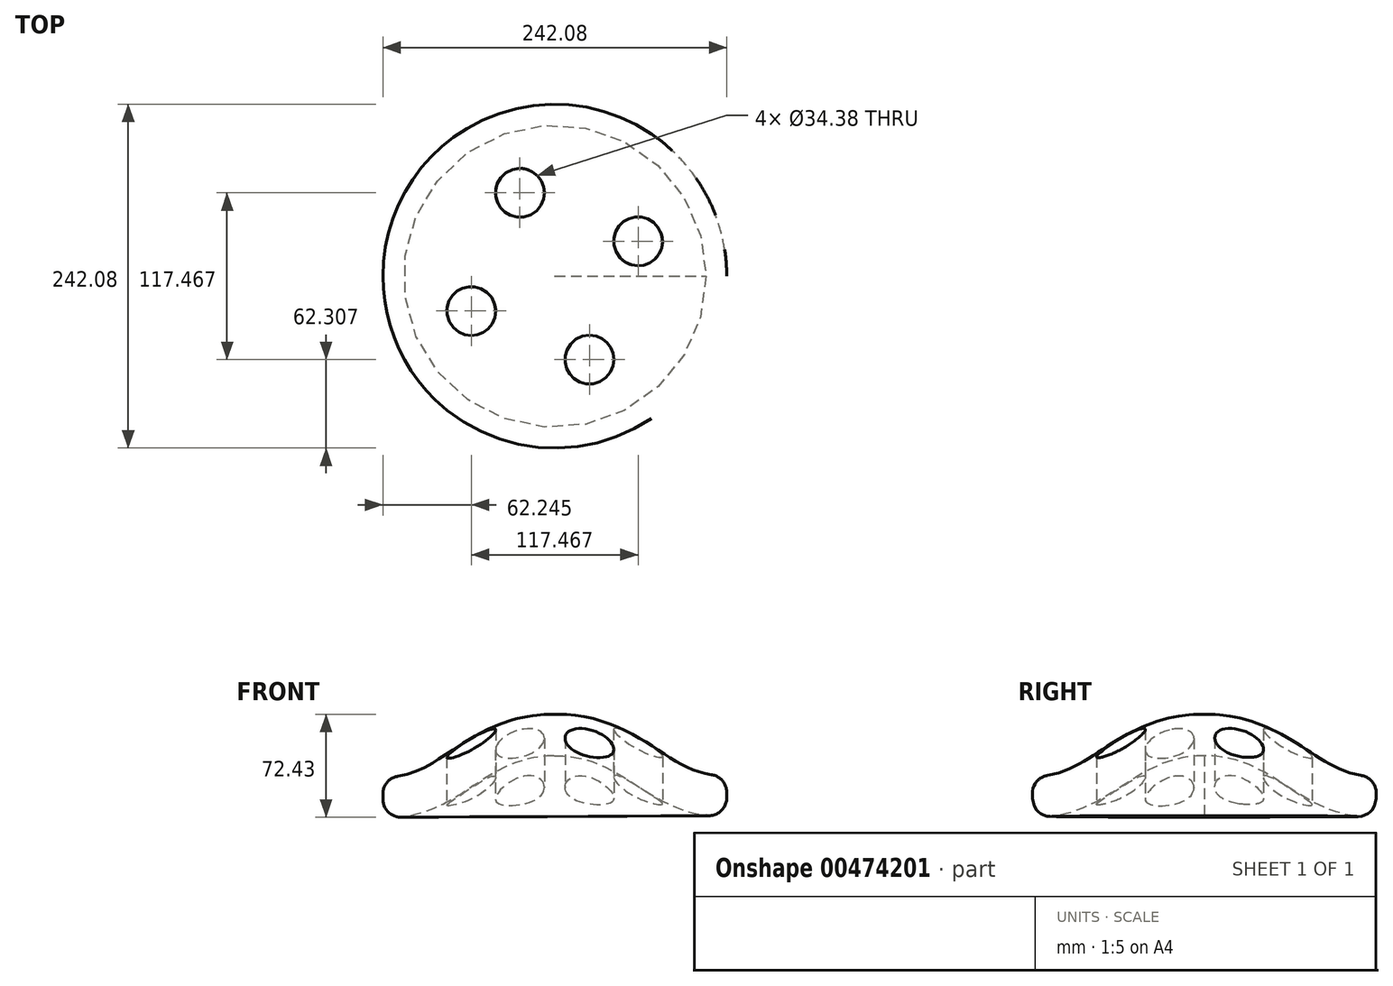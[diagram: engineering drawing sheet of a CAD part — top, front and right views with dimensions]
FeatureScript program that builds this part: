
annotation { "Feature Type Name" : "Feature", "Feature Type Description" : "" }
export const myFeature = defineFeature(function(context is Context, id is Id, definition is map)
    precondition{}
    {
        {
            var Q0;
            Q0=qCreatedBy(makeId("Front.planeOp"),FACE);
            var sketch = newSketch(context, id + "F0", { "sketchPlane" : qUnion([Q0])});
            skFitSpline(sketch, "E0", {"points": [v(-152.81, 0) * mm, v(-31.61, 43.06) * mm], "startDerivative": vector(155.87, -0.76) * mm, "endDerivative": vector(171.09, -0.36) * mm});
            skFitSpline(sketch, "E1.0", {"points": [v(-152.95, -29.15) * mm, v(-148.69, -29.17) * mm, v(-140.4, -28.76) * mm, v(-128.76, -26.9) * mm, v(-118.01, -23.95) * mm, v(-108.25, -20.2) * mm, v(-99.49, -15.95) * mm, v(-91.64, -11.5) * mm, v(-84.58, -7.09) * mm, v(-78.17, -2.92) * mm, v(-72.28, 0.89) * mm, v(-66.76, 4.23) * mm, v(-61.5, 7.07) * mm, v(-56.35, 9.42) * mm, v(-51.1, 11.3) * mm, v(-45.47, 12.73) * mm, v(-39.17, 13.68) * mm, v(-34.31, 13.92) * mm, v(-31.67, 13.91) * mm]});
            skLineSegment(sketch, "E2", {"start": v(-31.61, 43.06) * mm, "end": v(-31.67, 13.91) * mm});
            skLineSegment(sketch, "E3", {"start": v(-152.81, 0) * mm, "end": v(-152.95, -29.15) * mm});
            skSolve(sketch);
        }
        {
            var Q0;
            Q0=makeQuery(id+"F0.imprint","IMPRINT",FACE,{"disambiguationData":[TD([[makeQuery(id+"F0.imprint","IMPRINT",EDGE,{"derivedFrom":sQuery(id+"F0.wireOp",EDGE,"E0")}),-1.0]])]});
            var Q1;
            Q1=sQuery(id+"F0.wireOp",EDGE,"E3");
            revolve(context, id + "F1", {"entities" : qUnion([Q0]), "axis" : qUnion([Q1]), "revolveType" : RevolveType.FULL});
        }
        {
            var Q0;
            Q0=qCreatedBy(makeId("Top.planeOp"),FACE);
            var sketch = newSketch(context, id + "F2", { "sketchPlane" : qUnion([Q0])});
            skEllipse(sketch, "E4.0", {"center": v(-152.74, 0) * mm, "majorRadius": 121.07 * mm, "minorRadius": 121.07 * mm, "majorAxis": v(0, -1)});
            skCircle(sketch, "E5", {"center": v(-177.24, -58.73) * mm, "radius": 17.2 * mm});
            skCircle(sketch, "E6.1.0", {"center": v(-94, -24.5) * mm, "radius": 17.2 * mm});
            skCircle(sketch, "E6.2.0", {"center": v(-128.24, 58.73) * mm, "radius": 17.2 * mm});
            skCircle(sketch, "E7.1.3.0", {"center": v(-211.48, 24.5) * mm, "radius": 17.2 * mm});
            skSolve(sketch);
        }
        {
            var Q0;
            Q0=makeQuery(id+"F2.imprint","IMPRINT",FACE,{"disambiguationData":[TD([[makeQuery(id+"F2.imprint","IMPRINT",EDGE,{"derivedFrom":sQuery(id+"F2.wireOp",EDGE,"E6.2.0")}),1.0]])]});
            var Q1;
            Q1=makeQuery(id+"F2.imprint","IMPRINT",FACE,{"disambiguationData":[TD([[makeQuery(id+"F2.imprint","IMPRINT",EDGE,{"derivedFrom":sQuery(id+"F2.wireOp",EDGE,"E6.1.0")}),1.0]])]});
            var Q2;
            Q2=makeQuery(id+"F2.imprint","IMPRINT",FACE,{"disambiguationData":[TD([[makeQuery(id+"F2.imprint","IMPRINT",EDGE,{"derivedFrom":sQuery(id+"F2.wireOp",EDGE,"E5")}),1.0]])]});
            var Q3;
            Q3=makeQuery(id+"F2.imprint","IMPRINT",FACE,{"disambiguationData":[TD([[makeQuery(id+"F2.imprint","IMPRINT",EDGE,{"derivedFrom":sQuery(id+"F2.wireOp",EDGE,"E7.1.3.0")}),1.0]])]});
            extrude(context, id + "F3", {"entities" : qUnion([Q0, Q1, Q2, Q3]), "operationType" : NewBodyOperationType.REMOVE, "endBound" : BoundingType.SYMMETRIC, "oppositeDirection" : true, "depth" : 125.25 * mm});
        }
        {
            var Q0;
            Q0=makeQuery(id+"F1.opRevolve","SWEPT_EDGE",EDGE,{"disambiguationData":[OSD([sQuery(id+"F0.wireOp",EDGE,"E1.0"),sQuery(id+"F0.wireOp",EDGE,"E2")])]});
            var Q1;
            Q1=makeQuery(id+"F1.opRevolve","SWEPT_EDGE",EDGE,{"disambiguationData":[OSD([sQuery(id+"F0.wireOp",EDGE,"E0"),sQuery(id+"F0.wireOp",EDGE,"E2")])]});
            fillet(context, id + "F4", {"entities" : qUnion([Q0, Q1]), "radius" : 12.7 * mm, "tangentPropagation" : true, "allowEdgeOverflow" : false});
        }
        {
            var Q0;
            Q0=qCreatedBy(makeId("Front.planeOp"),FACE);
            var sketch = newSketch(context, id + "F5", { "sketchPlane" : qUnion([Q0])});
            skLineSegment(sketch, "E8", {"start": v(59.88, 11.44) * mm, "end": v(133.36, 11.44) * mm});
            skSolve(sketch);
        }
        {
            var Q0;
            Q0=makeQuery(id+"F1.opRevolve","SWEPT_BODY",BODY,{"disambiguationData":[OSD([sQuery(id+"F0.wireOp",EDGE,"E0"),sQuery(id+"F0.wireOp",EDGE,"E1.0"),sQuery(id+"F0.wireOp",EDGE,"E2"),sQuery(id+"F0.wireOp",EDGE,"E3")])]});
            var Q1;
            Q1=sQuery(id+"F5.wireOp",EDGE,"E8");
            transform(context, id + "F6", {"entities" : qUnion([Q0]), "transformType" : TransformType.ROTATION, "transformAxis" : qUnion([Q1]), "angle" : 180 * degree, "oppositeDirection" : true, "makeCopy" : false});
        }
    });
